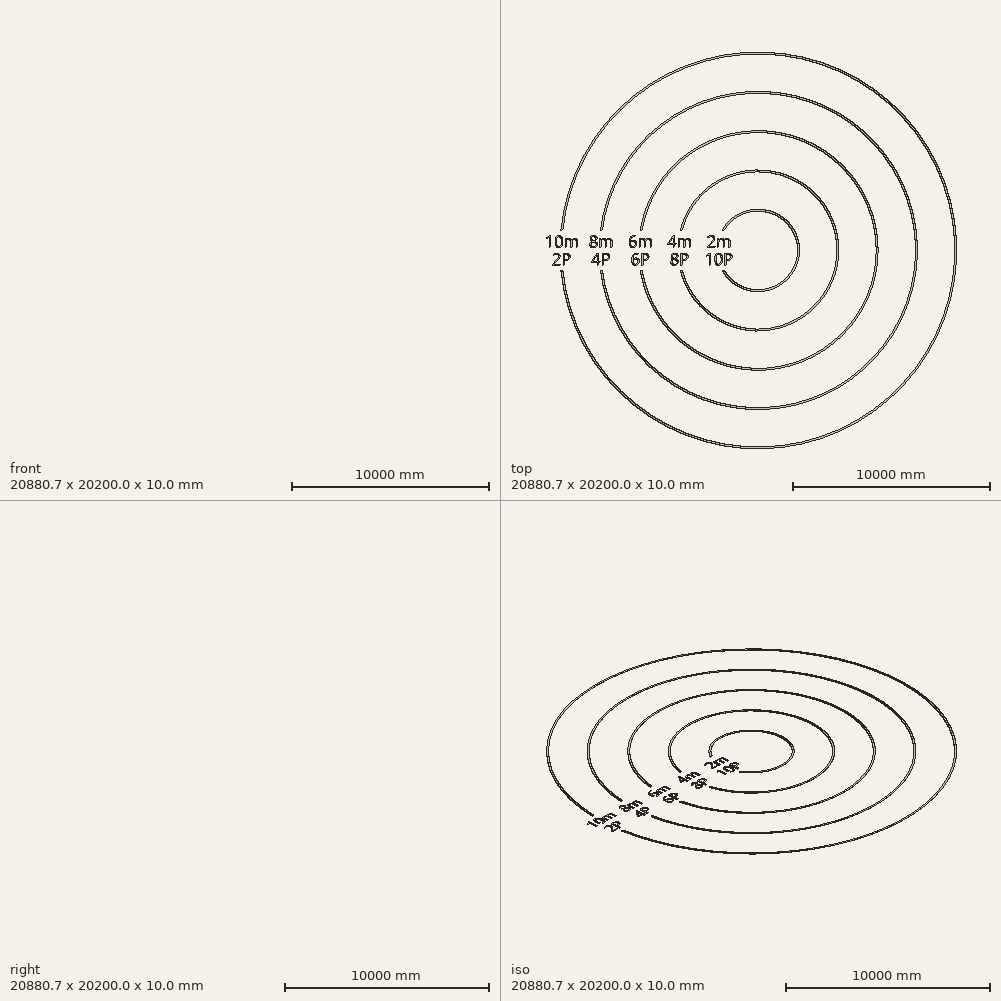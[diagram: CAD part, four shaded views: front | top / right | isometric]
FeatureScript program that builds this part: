
annotation { "Feature Type Name" : "Feature", "Feature Type Description" : "" }
export const myFeature = defineFeature(function(context is Context, id is Id, definition is map)
    precondition{}
    {
        {
            var Q0;
            Q0=qCreatedBy(makeId("Top.planeOp"),FACE);
            var sketch = newSketch(context, id + "F0", { "sketchPlane" : qUnion([Q0])});
            skCircle(sketch, "E0", {"center": v(0, 0) * mm, "radius": 50000 * mm});
            skCircle(sketch, "E1", {"center": v(0, 0) * mm, "radius": 40000 * mm});
            skCircle(sketch, "E2", {"center": v(0, 0) * mm, "radius": 30000 * mm});
            skCircle(sketch, "E3", {"center": v(0, 0) * mm, "radius": 20000 * mm});
            skCircle(sketch, "E4", {"center": v(0, 0) * mm, "radius": 10000 * mm});
            skCircle(sketch, "E5", {"center": v(0, 0) * mm, "radius": 8000 * mm});
            skCircle(sketch, "E6", {"center": v(0, 0) * mm, "radius": 6000 * mm});
            skCircle(sketch, "E7", {"center": v(0, 0) * mm, "radius": 4000 * mm});
            skCircle(sketch, "E8", {"center": v(0, 0) * mm, "radius": 2000 * mm});
            skCircle(sketch, "E9.0", {"center": v(0, 0) * mm, "radius": 50100 * mm});
            skCircle(sketch, "E10.0", {"center": v(0, 0) * mm, "radius": 40100 * mm});
            skCircle(sketch, "E11.0", {"center": v(0, 0) * mm, "radius": 30100 * mm});
            skCircle(sketch, "E12.0", {"center": v(0, 0) * mm, "radius": 20100 * mm});
            skCircle(sketch, "E13.0", {"center": v(0, 0) * mm, "radius": 10100 * mm});
            skCircle(sketch, "E14.0", {"center": v(0, 0) * mm, "radius": 8100 * mm});
            skCircle(sketch, "E15.0", {"center": v(0, 0) * mm, "radius": 6100 * mm});
            skCircle(sketch, "E16.0", {"center": v(0, 0) * mm, "radius": 4100 * mm});
            skCircle(sketch, "E17.0", {"center": v(0, 0) * mm, "radius": 2100 * mm});
            skSolve(sketch);
        }
        {
            var Q0;
            Q0=makeQuery(id+"F0.imprint","IMPRINT",FACE,{"disambiguationData":[TD([[makeQuery(id+"F0.imprint","IMPRINT",EDGE,{"derivedFrom":sQuery(id+"F0.wireOp",EDGE,"E4")}),-1.0]])]});
            var Q1;
            Q1=makeQuery(id+"F0.imprint","IMPRINT",FACE,{"disambiguationData":[TD([[makeQuery(id+"F0.imprint","IMPRINT",EDGE,{"derivedFrom":sQuery(id+"F0.wireOp",EDGE,"E5")}),-1.0]])]});
            var Q2;
            Q2=makeQuery(id+"F0.imprint","IMPRINT",FACE,{"disambiguationData":[TD([[makeQuery(id+"F0.imprint","IMPRINT",EDGE,{"derivedFrom":sQuery(id+"F0.wireOp",EDGE,"E6")}),-1.0]])]});
            var Q3;
            Q3=makeQuery(id+"F0.imprint","IMPRINT",FACE,{"disambiguationData":[TD([[makeQuery(id+"F0.imprint","IMPRINT",EDGE,{"derivedFrom":sQuery(id+"F0.wireOp",EDGE,"E7")}),-1.0]])]});
            var Q4;
            Q4=makeQuery(id+"F0.imprint","IMPRINT",FACE,{"disambiguationData":[TD([[makeQuery(id+"F0.imprint","IMPRINT",EDGE,{"derivedFrom":sQuery(id+"F0.wireOp",EDGE,"E8")}),-1.0]])]});
            extrude(context, id + "F1", {"entities" : qUnion([Q0, Q1, Q2, Q3, Q4]), "depth" : 10 * mm, "offsetDistance" : 25 * mm});
        }
        {
            var Q0;
            Q0=qCreatedBy(makeId("Top.planeOp"),FACE);
            var sketch = newSketch(context, id + "F2", { "sketchPlane" : qUnion([Q0])});
            skLineSegment(sketch, "E18.bottom", {"start": v(0, 1000) * mm, "end": v(-12000, 1000) * mm});
            skLineSegment(sketch, "E18.top", {"start": v(0, -1000) * mm, "end": v(-12000, -1000) * mm});
            skLineSegment(sketch, "E18.left", {"start": v(0, 1000) * mm, "end": v(0, -1000) * mm});
            skLineSegment(sketch, "E18.right", {"start": v(-12000, 1000) * mm, "end": v(-12000, -1000) * mm});
            skSolve(sketch);
        }
        {
            var Q0;
            Q0=qSketchRegion(id+"F2",true);
            extrude(context, id + "F3", {"entities" : qUnion([Q0]), "operationType" : NewBodyOperationType.REMOVE, "endBound" : BoundingType.THROUGH_ALL, "depth" : 25 * mm});
        }
        {
            var Q0;
            Q0=qCreatedBy(makeId("Top.planeOp"),FACE);
            var sketch = newSketch(context, id + "F4", { "sketchPlane" : qUnion([Q0])});
            skText(sketch, "E19", { "text": "2m", "fontName": "OpenSans-Regular.ttf"});
            skText(sketch, "E20", { "text": "4m", "fontName": "OpenSans-Regular.ttf"});
            skText(sketch, "E21", { "text": "6m", "fontName": "OpenSans-Regular.ttf"});
            skText(sketch, "E22", { "text": "8m", "fontName": "OpenSans-Regular.ttf"});
            skText(sketch, "E23", { "text": "10m", "fontName": "OpenSans-Regular.ttf"});
            skText(sketch, "E24", { "text": "10P", "fontName": "OpenSans-Regular.ttf"});
            skText(sketch, "E25", { "text": "8P", "fontName": "OpenSans-Regular.ttf"});
            skText(sketch, "E26", { "text": "6P", "fontName": "OpenSans-Regular.ttf"});
            skText(sketch, "E27", { "text": "4P", "fontName": "OpenSans-Regular.ttf"});
            skText(sketch, "E28", { "text": "2P", "fontName": "OpenSans-Regular.ttf"});
            const initialGuessF4  = {"E19": [-2.61901, 0.15, 1, 0, 0.6], "E20": [-4.61901, 0.15, 1, 0, 0.6], "E21": [-6.61901, 0.15, 1, 0, 0.6], "E22": [-8.61901, 0.15, 1, 0, 0.6], "E23": [-10.85723, 0.15, 1, 0, 0.6], "E24": [-2.73294, -0.75, 1, 0, 0.6], "E25": [-4.49473, -0.75, 1, 0, 0.6], "E26": [-6.49473, -0.75, 1, 0, 0.6], "E27": [-8.49473, -0.75, 1, 0, 0.6], "E28": [-10.49473, -0.75, 1, 0, 0.6]};
            skSetInitialGuess(sketch, initialGuessF4);
            skSolve(sketch);
        }
        {
            var Q0;
            Q0=qSketchRegion(id+"F4",true);
            var Q1;
            Q1=makeQuery(id+"F1.opExtrude","CAP_FACE",FACE,{"disambiguationData":[OSD([sQuery(id+"F0.wireOp",EDGE,"E8"),sQuery(id+"F0.wireOp",EDGE,"E17.0")])],"isStart":false});
            var Q2;
            Q2=makeQuery(id+"F1.opExtrude","SWEPT_BODY",BODY,{"disambiguationData":[OSD([sQuery(id+"F0.wireOp",EDGE,"E0"),sQuery(id+"F0.wireOp",EDGE,"E9.0")])]});
            extrude(context, id + "F5", {"entities" : qUnion([Q0]), "endBound" : BoundingType.UP_TO_SURFACE, "endBoundEntityFace" : qUnion([Q1]), "endBoundEntityBody" : qUnion([Q2]), "depth" : 25 * mm, "offsetDistance" : 25 * mm});
        }
    });
